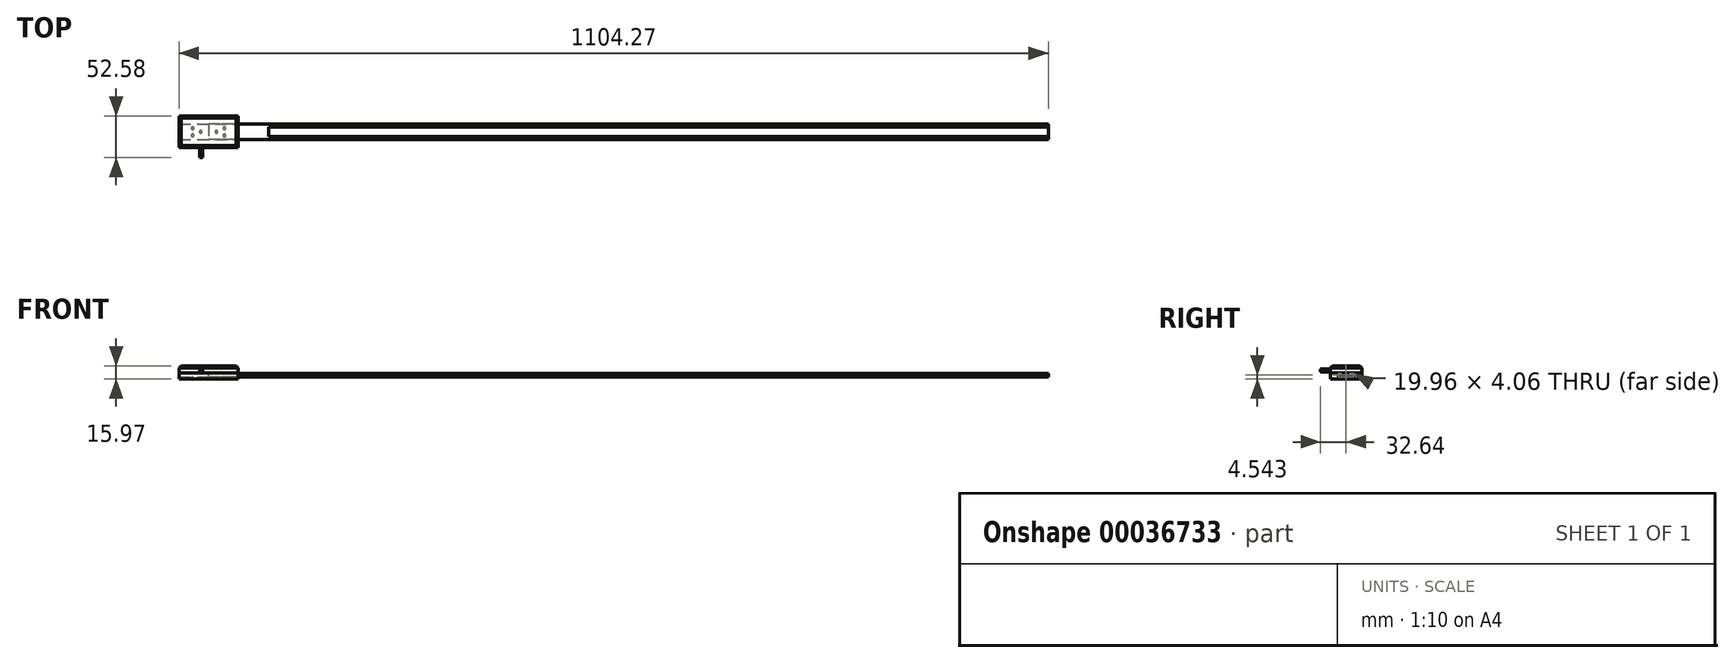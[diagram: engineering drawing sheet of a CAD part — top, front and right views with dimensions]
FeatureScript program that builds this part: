
annotation { "Feature Type Name" : "Feature", "Feature Type Description" : "" }
export const myFeature = defineFeature(function(context is Context, id is Id, definition is map)
    precondition{}
    {
        {
            var Q0;
            Q0=qCreatedBy(makeId("Top.planeOp"),FACE);
            var sketch = newSketch(context, id + "F0", { "sketchPlane" : qUnion([Q0])});
            skLineSegment(sketch, "E0.rect.bottom", {"start": v(37.47, 19.94) * mm, "end": v(-37.47, 19.94) * mm});
            skLineSegment(sketch, "E0.rect.top", {"start": v(37.47, -19.94) * mm, "end": v(-37.47, -19.94) * mm});
            skLineSegment(sketch, "E0.rect.left", {"start": v(37.47, 19.94) * mm, "end": v(37.47, -19.94) * mm});
            skLineSegment(sketch, "E0.rect.right", {"start": v(-37.47, 19.94) * mm, "end": v(-37.47, -19.94) * mm});
            skPoint(sketch, "E0.rect.middle", {"position": v(0, 0) * mm});
            skSolve(sketch);
        }
        {
            var Q0;
            Q0=makeQuery(id+"F0.imprint","IMPRINT",FACE,{"disambiguationData":[TD([[makeQuery(id+"F0.imprint","IMPRINT",EDGE,{"derivedFrom":sQuery(id+"F0.wireOp",EDGE,"E0.rect.bottom")}),1.0]])]});
            extrude(context, id + "F1", {"entities" : qUnion([Q0]), "oppositeDirection" : true, "depth" : 7.2 * mm});
        }
        {
            var Q0;
            Q0=makeQuery(id+"F1.opExtrude","CAP_FACE",FACE,{"disambiguationData":[OSD([sQuery(id+"F0.wireOp",EDGE,"E0.rect.bottom"),sQuery(id+"F0.wireOp",EDGE,"E0.rect.top"),sQuery(id+"F0.wireOp",EDGE,"E0.rect.left"),sQuery(id+"F0.wireOp",EDGE,"E0.rect.right")])],"isStart":true});
            var sketch = newSketch(context, id + "F2", { "sketchPlane" : qUnion([Q0])});
            skLineSegment(sketch, "E1.rect.bottom", {"start": v(37.47, 19.94) * mm, "end": v(-37.47, 19.94) * mm});
            skLineSegment(sketch, "E1.rect.top", {"start": v(37.47, -19.94) * mm, "end": v(-37.47, -19.94) * mm});
            skLineSegment(sketch, "E1.rect.left", {"start": v(37.47, 19.94) * mm, "end": v(37.47, -19.94) * mm});
            skLineSegment(sketch, "E1.rect.right", {"start": v(-37.47, 19.94) * mm, "end": v(-37.47, -19.94) * mm});
            skPoint(sketch, "E1.rect.middle", {"position": v(0, 0) * mm});
            skSolve(sketch);
        }
        {
            var Q0;
            Q0=makeQuery(id+"F2.imprint","IMPRINT",FACE,{"disambiguationData":[TD([[makeQuery(id+"F2.imprint","IMPRINT",EDGE,{"derivedFrom":sQuery(id+"F2.wireOp",EDGE,"E1.rect.bottom")}),1.0]])]});
            extrude(context, id + "F3", {"entities" : qUnion([Q0]), "depth" : 8.76 * mm});
        }
        {
            var Q0;
            Q0=makeQuery(id+"F3.opExtrude","CAP_FACE",FACE,{"disambiguationData":[OSD([sQuery(id+"F2.wireOp",EDGE,"E1.rect.bottom"),sQuery(id+"F2.wireOp",EDGE,"E1.rect.top"),sQuery(id+"F2.wireOp",EDGE,"E1.rect.left"),sQuery(id+"F2.wireOp",EDGE,"E1.rect.right")])],"isStart":false});
            chamfer(context, id + "F4", {"entities" : qUnion([Q0]), "width" : 2.54 * mm, "tangentPropagation" : true});
        }
        {
            var Q0;
            Q0=makeQuery(id+"F3.opExtrude","SWEPT_FACE",FACE,{"disambiguationData":[OSD([sQuery(id+"F2.wireOp",EDGE,"E1.rect.top")])]});
            var sketch = newSketch(context, id + "F5", { "sketchPlane" : qUnion([Q0])});
            skCircle(sketch, "E2", {"center": v(-9.53, 3.14) * mm, "radius": 1.9 * mm});
            skSolve(sketch);
        }
        {
            var Q0;
            Q0=makeQuery(id+"F5.imprint","IMPRINT",FACE,{"disambiguationData":[TD([[makeQuery(id+"F5.imprint","IMPRINT",EDGE,{"derivedFrom":sQuery(id+"F5.wireOp",EDGE,"E2")}),1.0]])]});
            extrude(context, id + "F6", {"entities" : qUnion([Q0]), "depth" : 12.7 * mm});
        }
        {
            var Q0;
            Q0=makeQuery(id+"F1.opExtrude","SWEPT_FACE",FACE,{"disambiguationData":[OSD([sQuery(id+"F0.wireOp",EDGE,"E0.rect.left")])]});
            var sketch = newSketch(context, id + "F7", { "sketchPlane" : qUnion([Q0])});
            skLineSegment(sketch, "E3.bottom", {"start": v(-9.98, -0.64) * mm, "end": v(9.98, -0.63) * mm});
            skLineSegment(sketch, "E3.top", {"start": v(-9.98, -4.7) * mm, "end": v(9.98, -4.7) * mm});
            skLineSegment(sketch, "E3.left", {"start": v(-9.98, -0.64) * mm, "end": v(-9.98, -4.7) * mm});
            skLineSegment(sketch, "E3.right", {"start": v(9.98, -0.63) * mm, "end": v(9.98, -4.7) * mm});
            skSolve(sketch);
        }
        {
            var Q0;
            Q0 = qSketchRegion(id + "F7", true);
            extrude(context, id + "F8", {"entities" : qUnion([Q0]), "operationType" : NewBodyOperationType.REMOVE, "endBound" : BoundingType.THROUGH_ALL, "oppositeDirection" : true, "depth" : 25.4 * mm});
        }
        {
            var Q0;
            Q0=makeQuery(id+"F1.opExtrude","CAP_FACE",FACE,{"disambiguationData":[OSD([sQuery(id+"F0.wireOp",EDGE,"E0.rect.bottom"),sQuery(id+"F0.wireOp",EDGE,"E0.rect.top"),sQuery(id+"F0.wireOp",EDGE,"E0.rect.left"),sQuery(id+"F0.wireOp",EDGE,"E0.rect.right")])],"isStart":false});
            var sketch = newSketch(context, id + "F9", { "sketchPlane" : qUnion([Q0])});
            skPoint(sketch, "E4", {"position": v(-20.2, 4.57) * mm});
            skPoint(sketch, "E5", {"position": v(-20.2, -4.57) * mm});
            skPoint(sketch, "E6", {"position": v(-10.03, 0) * mm});
            skPoint(sketch, "E7", {"position": v(10.03, 0) * mm});
            skPoint(sketch, "E8", {"position": v(20.2, 4.57) * mm});
            skPoint(sketch, "E9", {"position": v(20.2, -4.57) * mm});
            skSolve(sketch);
        }
        {
            var Q0;
            Q0=qCreatedBy(makeId("Right.planeOp"),FACE);
            var sketch = newSketch(context, id + "F10", { "sketchPlane" : qUnion([Q0])});
            skLineSegment(sketch, "E10.bottom", {"start": v(9.98, -4.67) * mm, "end": v(-9.98, -4.67) * mm});
            skLineSegment(sketch, "E10.top", {"start": v(9.98, -0.6) * mm, "end": v(-9.98, -0.6) * mm});
            skLineSegment(sketch, "E10.left", {"start": v(9.98, -4.67) * mm, "end": v(9.98, -0.6) * mm});
            skLineSegment(sketch, "E10.right", {"start": v(-9.98, -4.67) * mm, "end": v(-9.98, -0.6) * mm});
            skSolve(sketch);
        }
        {
            var Q0;
            Q0=makeQuery(id+"F10.imprint","IMPRINT",FACE,{"disambiguationData":[TD([[makeQuery(id+"F10.imprint","IMPRINT",EDGE,{"derivedFrom":sQuery(id+"F10.wireOp",EDGE,"E10.bottom")}),-1.0]])]});
            extrude(context, id + "F11", {"entities" : qUnion([Q0]), "depth" : 1066.8 * mm, "offsetDistance" : 25.4 * mm});
        }
        {
            var Q0;
            Q0=makeQuery(id+"F11.opExtrude","SWEPT_FACE",FACE,{"disambiguationData":[OSD([sQuery(id+"F10.wireOp",EDGE,"E10.top")])]});
            var sketch = newSketch(context, id + "F12", { "sketchPlane" : qUnion([Q0])});
            skLineSegment(sketch, "E11.bottom", {"start": v(1066.8, 6.17) * mm, "end": v(76.2, 6.17) * mm});
            skLineSegment(sketch, "E11.top", {"start": v(1066.8, -6.17) * mm, "end": v(76.2, -6.17) * mm});
            skLineSegment(sketch, "E11.left", {"start": v(1066.8, 6.17) * mm, "end": v(1066.8, -6.17) * mm});
            skLineSegment(sketch, "E11.right", {"start": v(76.2, 6.17) * mm, "end": v(76.2, -6.17) * mm});
            skSolve(sketch);
        }
        {
            var Q0;
            {var subQ8=sQuery(id+"F12.wireOp",EDGE,"E11.left");Q0=makeQuery(id+"F12.imprint","IMPRINT",FACE,{"disambiguationData":[TD([[makeQuery(id+"F12.imprint","IMPRINT",EDGE,{"derivedFrom":subQ8}),-1.0]])]});}
            extrude(context, id + "F13", {"entities" : qUnion([Q0]), "depth" : 0.25 * mm});
        }
        {
            var Q0;
            Q0=sQuery(id+"F9.wireOp",VERTEX,"E8");
            var Q1;
            Q1=sQuery(id+"F9.wireOp",VERTEX,"E9");
            var Q2;
            Q2=sQuery(id+"F9.wireOp",VERTEX,"E7");
            var Q3;
            Q3=sQuery(id+"F9.wireOp",VERTEX,"E6");
            var Q4;
            Q4=sQuery(id+"F9.wireOp",VERTEX,"E4");
            var Q5;
            Q5=sQuery(id+"F9.wireOp",VERTEX,"E5");
            var Q6;
            Q6=makeQuery(id+"F1.opExtrude","SWEPT_BODY",BODY,{"disambiguationData":[OSD([sQuery(id+"F0.wireOp",EDGE,"E0.rect.bottom"),sQuery(id+"F0.wireOp",EDGE,"E0.rect.top"),sQuery(id+"F0.wireOp",EDGE,"E0.rect.left"),sQuery(id+"F0.wireOp",EDGE,"E0.rect.right")])]});
            var Q7;
            Q7=makeQuery(id+"F3.opExtrude","SWEPT_BODY",BODY,{"disambiguationData":[OSD([sQuery(id+"F2.wireOp",EDGE,"E1.rect.bottom"),sQuery(id+"F2.wireOp",EDGE,"E1.rect.top"),sQuery(id+"F2.wireOp",EDGE,"E1.rect.left"),sQuery(id+"F2.wireOp",EDGE,"E1.rect.right")])]});
            var Q8;
            Q8=makeQuery(id+"F11.opExtrude","SWEPT_BODY",BODY,{"disambiguationData":[OSD([sQuery(id+"F10.wireOp",EDGE,"E10.bottom"),sQuery(id+"F10.wireOp",EDGE,"E10.top"),sQuery(id+"F10.wireOp",EDGE,"E10.left"),sQuery(id+"F10.wireOp",EDGE,"E10.right")])]});
            var Q9;
            Q9=makeQuery(id+"F13.opExtrude","SWEPT_BODY",BODY,{"disambiguationData":[OSD([sQuery(id+"F12.wireOp",EDGE,"E11.bottom"),sQuery(id+"F12.wireOp",EDGE,"E11.top"),sQuery(id+"F12.wireOp",EDGE,"E11.left"),sQuery(id+"F12.wireOp",EDGE,"E11.right")])]});
            hole(context, id + "F14", {"style" : HoleStyle.SIMPLE, "endStyle" : HoleEndStyle.BLIND, "standardTappedOrClearance" : lookupTablePath({ "standard" : "ISO", "fit" : "Normal", "size" : "M3", "type" : "Clearance" }), "standardBlindInLast" : lookupTablePath({ "fit" : "Standard", "standard" : "ISO", "size" : "M3", "type" : "Clearance" }), "holeDiameter" : 3.3 * mm, "holeDepth" : 1.27 * mm, "tappedDepth" : 6.35 * mm, "tapClearance" : 3, "locations" : qUnion([Q0, Q1, Q2, Q3, Q4, Q5]), "scope" : qUnion([Q6, Q7, Q8, Q9])});
        }
    });
